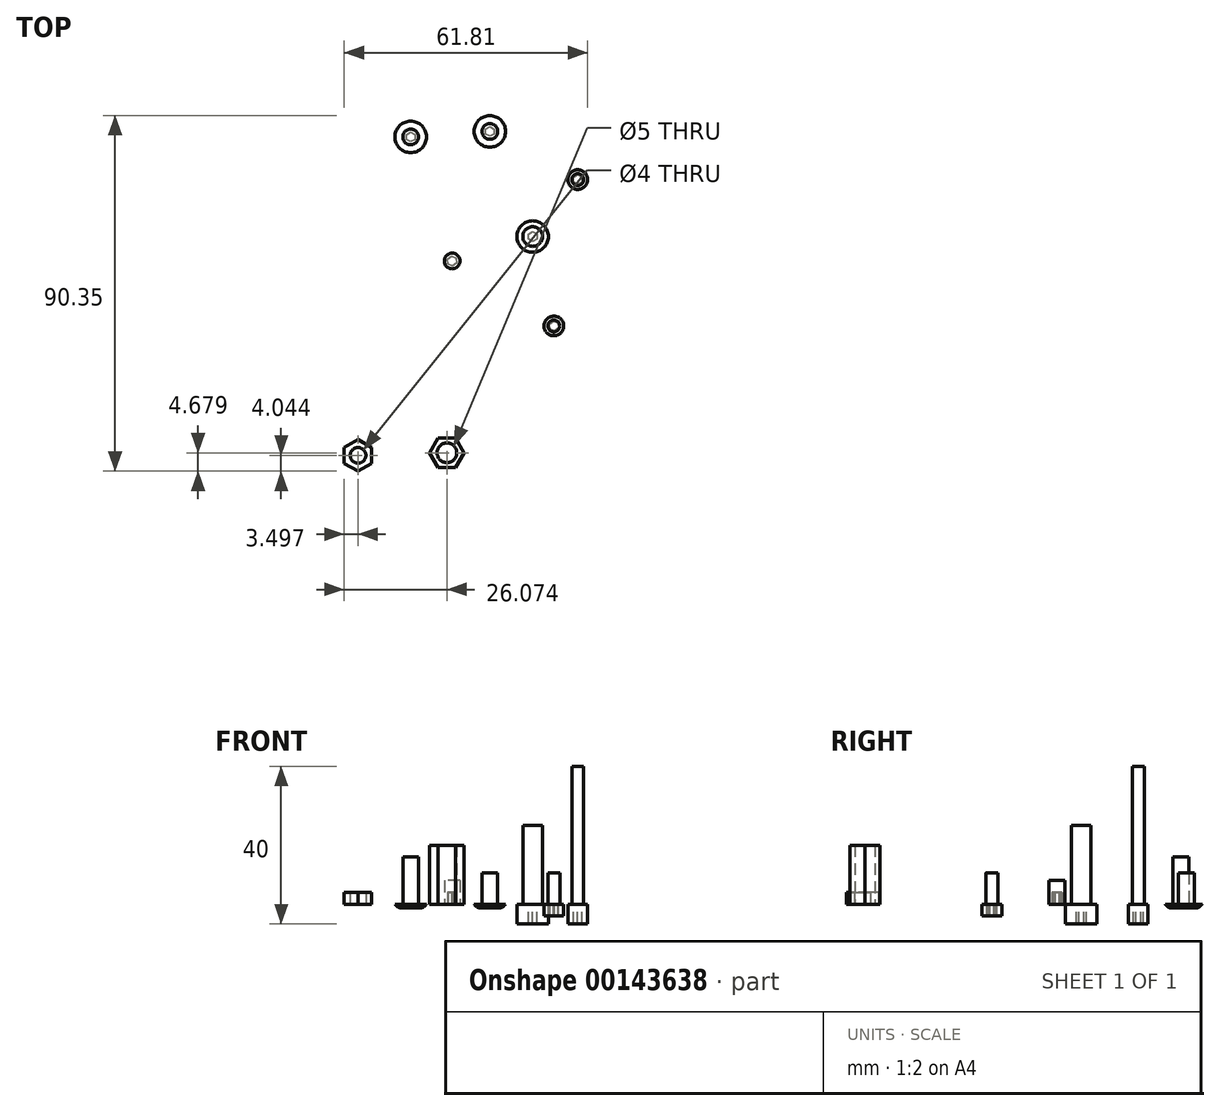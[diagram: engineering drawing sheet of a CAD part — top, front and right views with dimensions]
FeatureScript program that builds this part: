
annotation { "Feature Type Name" : "Feature", "Feature Type Description" : "" }
export const myFeature = defineFeature(function(context is Context, id is Id, definition is map)
    precondition{}
    {
        {
            var Q0;
            Q0=qCreatedBy(makeId("Top.planeOp"),FACE);
            var sketch = newSketch(context, id + "F0", { "sketchPlane" : qUnion([Q0])});
            skCircle(sketch, "E0.cCircle", {"center": v(25.66, -16.3) * mm, "radius": 1.25 * mm, "construction": true});
            skLineSegment(sketch, "E0.0", {"start": v(25.54, -15.06) * mm, "end": v(26.68, -15.57) * mm});
            skLineSegment(sketch, "E0.1", {"start": v(26.68, -15.57) * mm, "end": v(26.8, -16.82) * mm});
            skLineSegment(sketch, "E0.2", {"start": v(26.8, -16.82) * mm, "end": v(25.78, -17.55) * mm});
            skLineSegment(sketch, "E0.3", {"start": v(25.78, -17.55) * mm, "end": v(24.64, -17.03) * mm});
            skLineSegment(sketch, "E0.4", {"start": v(24.64, -17.03) * mm, "end": v(24.52, -15.79) * mm});
            skLineSegment(sketch, "E0.5", {"start": v(24.52, -15.79) * mm, "end": v(25.54, -15.06) * mm});
            skCircle(sketch, "E1.cCircle", {"center": v(9.4, 33.13) * mm, "radius": 1.25 * mm, "construction": true});
            skLineSegment(sketch, "E1.0", {"start": v(9.4, 34.38) * mm, "end": v(10.48, 33.75) * mm});
            skLineSegment(sketch, "E1.1", {"start": v(10.48, 33.75) * mm, "end": v(10.48, 32.5) * mm});
            skLineSegment(sketch, "E1.2", {"start": v(10.48, 32.5) * mm, "end": v(9.4, 31.88) * mm});
            skLineSegment(sketch, "E1.3", {"start": v(9.4, 31.88) * mm, "end": v(8.31, 32.5) * mm});
            skLineSegment(sketch, "E1.4", {"start": v(8.31, 32.5) * mm, "end": v(8.31, 33.75) * mm});
            skLineSegment(sketch, "E1.5", {"start": v(8.31, 33.75) * mm, "end": v(9.4, 34.38) * mm});
            skCircle(sketch, "E2.cCircle", {"center": v(20.27, 6.42) * mm, "radius": 1.25 * mm, "construction": true});
            skLineSegment(sketch, "E2.0", {"start": v(20.27, 7.67) * mm, "end": v(21.35, 7.04) * mm});
            skLineSegment(sketch, "E2.1", {"start": v(21.35, 7.04) * mm, "end": v(21.35, 5.8) * mm});
            skLineSegment(sketch, "E2.2", {"start": v(21.35, 5.8) * mm, "end": v(20.27, 5.17) * mm});
            skLineSegment(sketch, "E2.3", {"start": v(20.27, 5.17) * mm, "end": v(19.18, 5.8) * mm});
            skLineSegment(sketch, "E2.4", {"start": v(19.18, 5.8) * mm, "end": v(19.18, 7.04) * mm});
            skLineSegment(sketch, "E2.5", {"start": v(19.18, 7.04) * mm, "end": v(20.27, 7.67) * mm});
            skCircle(sketch, "E3.cCircle", {"center": v(31.72, 20.88) * mm, "radius": 1.25 * mm, "construction": true});
            skLineSegment(sketch, "E3.0", {"start": v(31.72, 22.13) * mm, "end": v(32.8, 21.5) * mm});
            skLineSegment(sketch, "E3.1", {"start": v(32.8, 21.5) * mm, "end": v(32.8, 20.26) * mm});
            skLineSegment(sketch, "E3.2", {"start": v(32.8, 20.26) * mm, "end": v(31.72, 19.63) * mm});
            skLineSegment(sketch, "E3.3", {"start": v(31.72, 19.63) * mm, "end": v(30.64, 20.26) * mm});
            skLineSegment(sketch, "E3.4", {"start": v(30.64, 20.26) * mm, "end": v(30.64, 21.5) * mm});
            skLineSegment(sketch, "E3.5", {"start": v(30.64, 21.5) * mm, "end": v(31.72, 22.13) * mm});
            skCircle(sketch, "E4", {"center": v(25.66, -16.3) * mm, "radius": 2.5 * mm});
            skCircle(sketch, "E5", {"center": v(25.66, -16.3) * mm, "radius": 1.5 * mm});
            skCircle(sketch, "E6", {"center": v(20.27, 6.42) * mm, "radius": 2.5 * mm});
            skCircle(sketch, "E7", {"center": v(20.27, 6.42) * mm, "radius": 4 * mm});
            skCircle(sketch, "E8", {"center": v(9.4, 33.13) * mm, "radius": 4 * mm});
            skCircle(sketch, "E9", {"center": v(9.4, 33.13) * mm, "radius": 2 * mm});
            skLineSegment(sketch, "E10.0", {"start": v(-0.3, 1.45) * mm, "end": v(0.85, 0.94) * mm});
            skLineSegment(sketch, "E10.1", {"start": v(0.85, 0.94) * mm, "end": v(0.97, -0.3) * mm});
            skLineSegment(sketch, "E10.2", {"start": v(0.97, -0.3) * mm, "end": v(-0.05, -1.04) * mm});
            skLineSegment(sketch, "E10.3", {"start": v(-0.05, -1.04) * mm, "end": v(-1.18, -0.52) * mm});
            skLineSegment(sketch, "E10.4", {"start": v(-1.18, -0.52) * mm, "end": v(-1.3, 0.72) * mm});
            skLineSegment(sketch, "E10.5", {"start": v(-1.3, 0.72) * mm, "end": v(-0.3, 1.45) * mm});
            skCircle(sketch, "E11", {"center": v(-0.17, 0.2) * mm, "radius": 2 * mm});
            skCircle(sketch, "E12", {"center": v(31.72, 20.88) * mm, "radius": 1.5 * mm});
            skCircle(sketch, "E13", {"center": v(31.72, 20.88) * mm, "radius": 2.5 * mm});
            skCircle(sketch, "E14.cCircle", {"center": v(-24.1, -49.18) * mm, "radius": 3.5 * mm, "construction": true});
            skLineSegment(sketch, "E14.0", {"start": v(-20.6, -47.16) * mm, "end": v(-20.6, -51.2) * mm});
            skLineSegment(sketch, "E14.1", {"start": v(-20.6, -51.2) * mm, "end": v(-24.1, -53.22) * mm});
            skLineSegment(sketch, "E14.2", {"start": v(-24.1, -53.22) * mm, "end": v(-27.6, -51.2) * mm});
            skLineSegment(sketch, "E14.3", {"start": v(-27.6, -51.2) * mm, "end": v(-27.6, -47.16) * mm});
            skLineSegment(sketch, "E14.4", {"start": v(-27.6, -47.16) * mm, "end": v(-24.1, -45.13) * mm});
            skLineSegment(sketch, "E14.5", {"start": v(-24.1, -45.13) * mm, "end": v(-20.6, -47.16) * mm});
            skPoint(sketch, "E14.0.midPoint", {"position": v(-20.6, -49.18) * mm});
            skCircle(sketch, "E15", {"center": v(-24.1, -49.18) * mm, "radius": 2 * mm});
            skCircle(sketch, "E16.cCircle", {"center": v(-10.72, 31.73) * mm, "radius": 1.25 * mm, "construction": true});
            skLineSegment(sketch, "E16.0", {"start": v(-10.72, 32.98) * mm, "end": v(-9.63, 32.35) * mm});
            skLineSegment(sketch, "E16.1", {"start": v(-9.63, 32.35) * mm, "end": v(-9.63, 31.1) * mm});
            skLineSegment(sketch, "E16.2", {"start": v(-9.63, 31.1) * mm, "end": v(-10.72, 30.48) * mm});
            skLineSegment(sketch, "E16.3", {"start": v(-10.72, 30.48) * mm, "end": v(-11.8, 31.1) * mm});
            skLineSegment(sketch, "E16.4", {"start": v(-11.8, 31.1) * mm, "end": v(-11.8, 32.35) * mm});
            skLineSegment(sketch, "E16.5", {"start": v(-11.8, 32.35) * mm, "end": v(-10.72, 32.98) * mm});
            skCircle(sketch, "E17", {"center": v(-10.72, 31.73) * mm, "radius": 4 * mm});
            skCircle(sketch, "E18", {"center": v(-10.72, 31.73) * mm, "radius": 2 * mm});
            skCircle(sketch, "E19", {"center": v(-1.52, -48.54) * mm, "radius": 2.5 * mm});
            skCircle(sketch, "E20.cCircle", {"center": v(-1.52, -48.54) * mm, "radius": 4.38 * mm, "construction": true});
            skLineSegment(sketch, "E20.0", {"start": v(2.86, -48.54) * mm, "end": v(0.67, -52.33) * mm});
            skLineSegment(sketch, "E20.1", {"start": v(0.67, -52.33) * mm, "end": v(-3.7, -52.33) * mm});
            skLineSegment(sketch, "E20.2", {"start": v(-3.7, -52.33) * mm, "end": v(-5.9, -48.54) * mm});
            skLineSegment(sketch, "E20.3", {"start": v(-5.9, -48.54) * mm, "end": v(-3.7, -44.75) * mm});
            skLineSegment(sketch, "E20.4", {"start": v(-3.7, -44.75) * mm, "end": v(0.67, -44.75) * mm});
            skLineSegment(sketch, "E20.5", {"start": v(0.67, -44.75) * mm, "end": v(2.86, -48.54) * mm});
            skSolve(sketch);
        }
        {
            var Q0;
            Q0=makeQuery(id+"F0.imprint","IMPRINT",FACE,{"disambiguationData":[TD([[makeQuery(id+"F0.imprint","IMPRINT",EDGE,{"derivedFrom":sQuery(id+"F0.wireOp",EDGE,"E10.0")}),-1.0]])]});
            var Q1;
            Q1=makeQuery(id+"F0.imprint","IMPRINT",FACE,{"disambiguationData":[TD([[makeQuery(id+"F0.imprint","IMPRINT",EDGE,{"derivedFrom":sQuery(id+"F0.wireOp",EDGE,"E10.0")}),1.0]])]});
            extrude(context, id + "F1", {"entities" : qUnion([Q0, Q1]), "depth" : 6 * mm});
        }
        {
            var Q0;
            Q0=makeQuery(id+"F0.imprint","IMPRINT",FACE,{"disambiguationData":[TD([[makeQuery(id+"F0.imprint","IMPRINT",EDGE,{"derivedFrom":sQuery(id+"F0.wireOp",EDGE,"E0.0")}),1.0]])]});
            var Q1;
            Q1=makeQuery(id+"F0.imprint","IMPRINT",FACE,{"disambiguationData":[TD([[makeQuery(id+"F0.imprint","IMPRINT",EDGE,{"derivedFrom":sQuery(id+"F0.wireOp",EDGE,"E0.0")}),-1.0]])]});
            extrude(context, id + "F2", {"entities" : qUnion([Q0, Q1]), "depth" : 8 * mm});
        }
        {
            var Q0;
            Q0=makeQuery(id+"F0.imprint","IMPRINT",FACE,{"disambiguationData":[TD([[makeQuery(id+"F0.imprint","IMPRINT",EDGE,{"derivedFrom":sQuery(id+"F0.wireOp",EDGE,"E4")}),1.0]])]});
            var Q1;
            Q1=makeQuery(id+"F0.imprint","IMPRINT",FACE,{"disambiguationData":[TD([[makeQuery(id+"F0.imprint","IMPRINT",EDGE,{"derivedFrom":sQuery(id+"F0.wireOp",EDGE,"E0.0")}),1.0]])]});
            extrude(context, id + "F3", {"entities" : qUnion([Q0, Q1]), "operationType" : NewBodyOperationType.ADD, "oppositeDirection" : true, "depth" : 3 * mm});
        }
        {
            var Q0;
            Q0=makeQuery(id+"F0.imprint","IMPRINT",FACE,{"disambiguationData":[TD([[makeQuery(id+"F0.imprint","IMPRINT",EDGE,{"derivedFrom":sQuery(id+"F0.wireOp",EDGE,"E2.0")}),1.0]])]});
            var Q1;
            Q1=makeQuery(id+"F0.imprint","IMPRINT",FACE,{"disambiguationData":[TD([[makeQuery(id+"F0.imprint","IMPRINT",EDGE,{"derivedFrom":sQuery(id+"F0.wireOp",EDGE,"E2.0")}),-1.0]])]});
            extrude(context, id + "F4", {"entities" : qUnion([Q0, Q1]), "depth" : 20 * mm});
        }
        {
            var Q0;
            Q0=makeQuery(id+"F0.imprint","IMPRINT",FACE,{"disambiguationData":[TD([[makeQuery(id+"F0.imprint","IMPRINT",EDGE,{"derivedFrom":sQuery(id+"F0.wireOp",EDGE,"E6")}),-1.0]])]});
            var Q1;
            Q1=makeQuery(id+"F0.imprint","IMPRINT",FACE,{"disambiguationData":[TD([[makeQuery(id+"F0.imprint","IMPRINT",EDGE,{"derivedFrom":sQuery(id+"F0.wireOp",EDGE,"E2.0")}),1.0]])]});
            var Q2;
            Q2=makeQuery(id+"F0.imprint","IMPRINT",FACE,{"disambiguationData":[TD([[makeQuery(id+"F0.imprint","IMPRINT",EDGE,{"derivedFrom":sQuery(id+"F0.wireOp",EDGE,"E12")}),-1.0]])]});
            var Q3;
            Q3=makeQuery(id+"F0.imprint","IMPRINT",FACE,{"disambiguationData":[TD([[makeQuery(id+"F0.imprint","IMPRINT",EDGE,{"derivedFrom":sQuery(id+"F0.wireOp",EDGE,"E3.0")}),1.0]])]});
            extrude(context, id + "F5", {"entities" : qUnion([Q0, Q1, Q2, Q3]), "operationType" : NewBodyOperationType.ADD, "oppositeDirection" : true, "depth" : 5 * mm});
        }
        {
            var Q0;
            Q0=makeQuery(id+"F0.imprint","IMPRINT",FACE,{"disambiguationData":[TD([[makeQuery(id+"F0.imprint","IMPRINT",EDGE,{"derivedFrom":sQuery(id+"F0.wireOp",EDGE,"E10.0")}),-1.0]])]});
            extrude(context, id + "F6", {"entities" : qUnion([Q0]), "operationType" : NewBodyOperationType.REMOVE, "depth" : 3 * mm});
        }
        {
            var Q0;
            Q0=makeQuery(id+"F0.imprint","IMPRINT",FACE,{"disambiguationData":[TD([[makeQuery(id+"F0.imprint","IMPRINT",EDGE,{"derivedFrom":sQuery(id+"F0.wireOp",EDGE,"E1.0")}),1.0]])]});
            var Q1;
            Q1=makeQuery(id+"F0.imprint","IMPRINT",FACE,{"disambiguationData":[TD([[makeQuery(id+"F0.imprint","IMPRINT",EDGE,{"derivedFrom":sQuery(id+"F0.wireOp",EDGE,"E1.0")}),-1.0]])]});
            extrude(context, id + "F7", {"entities" : qUnion([Q0, Q1]), "depth" : 8 * mm});
        }
        {
            var Q0;
            Q0=makeQuery(id+"F0.imprint","IMPRINT",FACE,{"disambiguationData":[TD([[makeQuery(id+"F0.imprint","IMPRINT",EDGE,{"derivedFrom":sQuery(id+"F0.wireOp",EDGE,"E8")}),1.0]])]});
            var Q1;
            Q1=makeQuery(id+"F0.imprint","IMPRINT",FACE,{"disambiguationData":[TD([[makeQuery(id+"F0.imprint","IMPRINT",EDGE,{"derivedFrom":sQuery(id+"F0.wireOp",EDGE,"E1.0")}),1.0]])]});
            var Q2;
            Q2=makeQuery(id+"F0.imprint","IMPRINT",FACE,{"disambiguationData":[TD([[makeQuery(id+"F0.imprint","IMPRINT",EDGE,{"derivedFrom":sQuery(id+"F0.wireOp",EDGE,"E17")}),1.0]])]});
            var Q3;
            Q3=makeQuery(id+"F0.imprint","IMPRINT",FACE,{"disambiguationData":[TD([[makeQuery(id+"F0.imprint","IMPRINT",EDGE,{"derivedFrom":sQuery(id+"F0.wireOp",EDGE,"E16.0")}),1.0]])]});
            extrude(context, id + "F8", {"entities" : qUnion([Q0, Q1, Q2, Q3]), "operationType" : NewBodyOperationType.ADD, "oppositeDirection" : true, "depth" : 1 * mm});
        }
        {
            var Q0;
            Q0=makeQuery(id+"F8.opExtrude","CAP_EDGE",EDGE,{"disambiguationData":[OSD([sQuery(id+"F0.wireOp",EDGE,"E8")])],"isStart":false});
            var Q1;
            Q1=makeQuery(id+"F8.opExtrude","CAP_EDGE",EDGE,{"disambiguationData":[OSD([sQuery(id+"F0.wireOp",EDGE,"E17")])],"isStart":false});
            fillet(context, id + "F9", {"entities" : qUnion([Q0, Q1]), "radius" : 2 * mm, "tangentPropagation" : true, "allowEdgeOverflow" : false});
        }
        {
            var Q0;
            Q0=makeQuery(id+"F0.imprint","IMPRINT",FACE,{"disambiguationData":[TD([[makeQuery(id+"F0.imprint","IMPRINT",EDGE,{"derivedFrom":sQuery(id+"F0.wireOp",EDGE,"E3.0")}),-1.0]])]});
            var Q1;
            Q1=makeQuery(id+"F0.imprint","IMPRINT",FACE,{"disambiguationData":[TD([[makeQuery(id+"F0.imprint","IMPRINT",EDGE,{"derivedFrom":sQuery(id+"F0.wireOp",EDGE,"E3.0")}),1.0]])]});
            extrude(context, id + "F10", {"entities" : qUnion([Q0, Q1]), "operationType" : NewBodyOperationType.ADD, "depth" : 35 * mm});
        }
        {
            var Q0;
            Q0=makeQuery(id+"F0.imprint","IMPRINT",FACE,{"disambiguationData":[TD([[makeQuery(id+"F0.imprint","IMPRINT",EDGE,{"derivedFrom":sQuery(id+"F0.wireOp",EDGE,"E14.0")}),-1.0]])]});
            extrude(context, id + "F11", {"entities" : qUnion([Q0]), "depth" : 3 * mm});
        }
        {
            var Q0;
            Q0=makeQuery(id+"F0.imprint","IMPRINT",FACE,{"disambiguationData":[TD([[makeQuery(id+"F0.imprint","IMPRINT",EDGE,{"derivedFrom":sQuery(id+"F0.wireOp",EDGE,"E16.0")}),-1.0]])]});
            var Q1;
            Q1=makeQuery(id+"F0.imprint","IMPRINT",FACE,{"disambiguationData":[TD([[makeQuery(id+"F0.imprint","IMPRINT",EDGE,{"derivedFrom":sQuery(id+"F0.wireOp",EDGE,"E16.0")}),1.0]])]});
            extrude(context, id + "F12", {"entities" : qUnion([Q0, Q1]), "operationType" : NewBodyOperationType.ADD, "depth" : 12 * mm});
        }
        {
            var Q0;
            Q0=makeQuery(id+"F0.imprint","IMPRINT",FACE,{"disambiguationData":[TD([[makeQuery(id+"F0.imprint","IMPRINT",EDGE,{"derivedFrom":sQuery(id+"F0.wireOp",EDGE,"E19")}),-1.0]])]});
            extrude(context, id + "F13", {"entities" : qUnion([Q0]), "depth" : 15 * mm});
        }
    });
